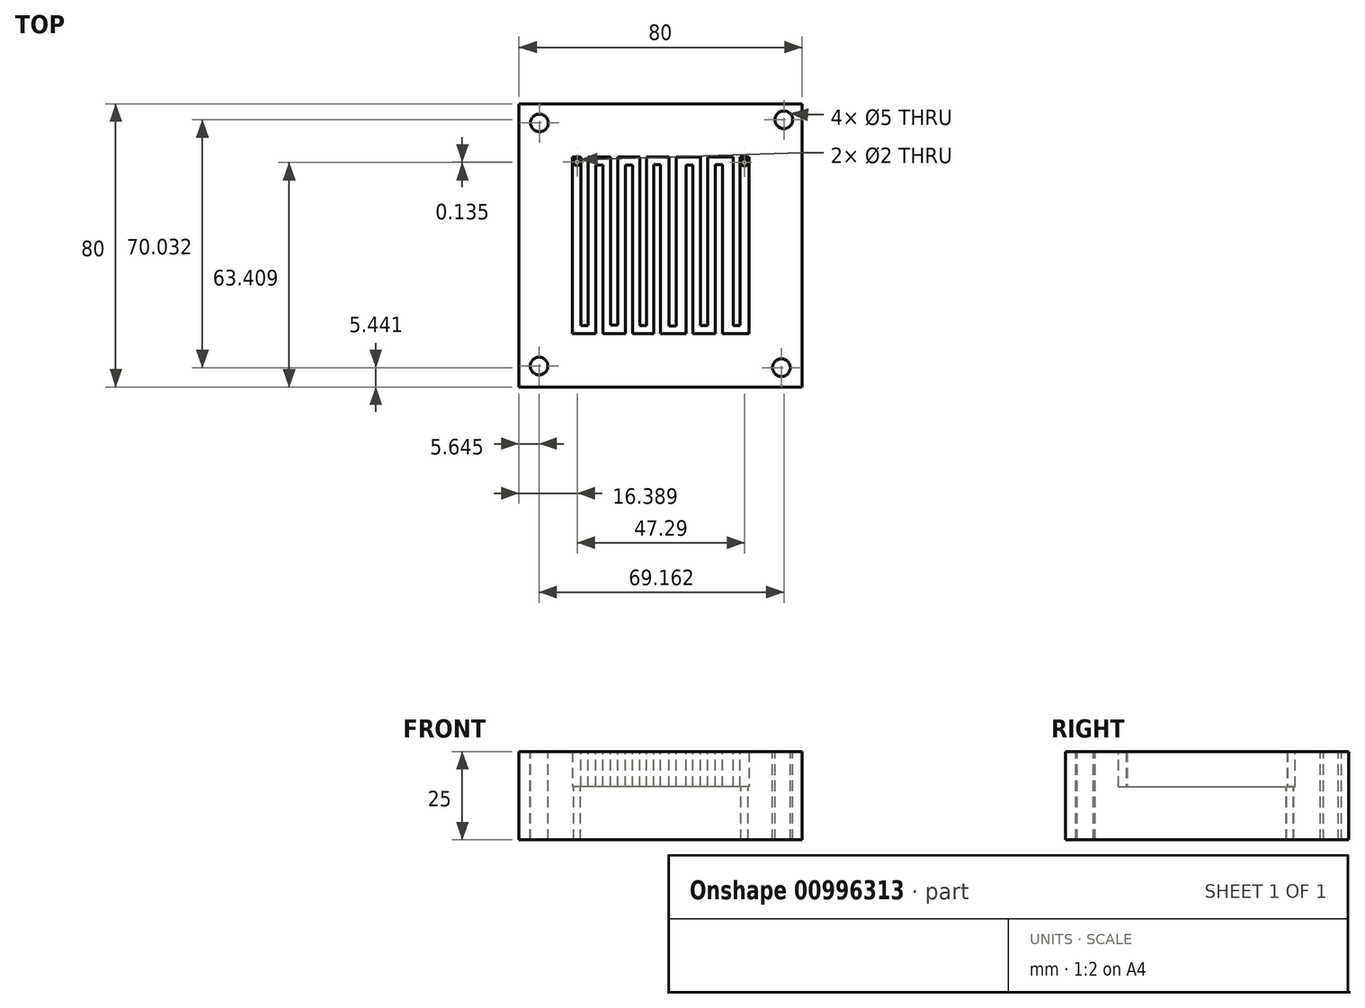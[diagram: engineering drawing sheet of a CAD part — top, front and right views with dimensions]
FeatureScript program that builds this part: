
annotation { "Feature Type Name" : "Feature", "Feature Type Description" : "" }
export const myFeature = defineFeature(function(context is Context, id is Id, definition is map)
    precondition{}
    {
        {
            var Q0;
            Q0=qCreatedBy(makeId("Top.planeOp"),FACE);
            var sketch = newSketch(context, id + "F0", { "sketchPlane" : qUnion([Q0])});
            skLineSegment(sketch, "E0.bottom", {"start": v(40, -40) * mm, "end": v(-40, -40) * mm});
            skLineSegment(sketch, "E0.top", {"start": v(40, 40) * mm, "end": v(-40, 40) * mm});
            skLineSegment(sketch, "E0.left", {"start": v(40, -40) * mm, "end": v(40, 40) * mm});
            skLineSegment(sketch, "E0.right", {"start": v(-40, -40) * mm, "end": v(-40, 40) * mm});
            skPoint(sketch, "E0.middle", {"position": v(0, 0) * mm});
            skSolve(sketch);
        }
        {
            var Q0;
            Q0=makeQuery(id+"F0.imprint","IMPRINT",FACE,{"disambiguationData":[TD([[makeQuery(id+"F0.imprint","IMPRINT",EDGE,{"derivedFrom":sQuery(id+"F0.wireOp",EDGE,"E0.bottom")}),-1.0]])]});
            var sketch = newSketch(context, id + "F1", { "sketchPlane" : qUnion([Q0])});
            skLineSegment(sketch, "E1.bottom", {"start": v(-22.53, 25.3) * mm, "end": v(-20.53, 25.3) * mm});
            skLineSegment(sketch, "E1.top", {"start": v(-22.53, -22.7) * mm, "end": v(-20.53, -22.7) * mm});
            skLineSegment(sketch, "E1.left", {"start": v(-22.53, 25.3) * mm, "end": v(-22.53, -22.7) * mm});
            skLineSegment(sketch, "E1.right", {"start": v(-20.53, 25.3) * mm, "end": v(-20.53, -22.7) * mm});
            skSolve(sketch);
        }
        {
            var Q0;
            Q0=makeQuery(id+"F0.imprint","IMPRINT",FACE,{"disambiguationData":[TD([[makeQuery(id+"F0.imprint","IMPRINT",EDGE,{"derivedFrom":sQuery(id+"F0.wireOp",EDGE,"E0.bottom")}),-1.0]])]});
            var sketch = newSketch(context, id + "F2", { "sketchPlane" : qUnion([Q0])});
            skLineSegment(sketch, "E2.bottom", {"start": v(-18.36, 22.64) * mm, "end": v(-16.36, 22.64) * mm});
            skLineSegment(sketch, "E2.top", {"start": v(-18.36, -25.36) * mm, "end": v(-16.36, -25.36) * mm});
            skLineSegment(sketch, "E2.left", {"start": v(-18.36, 22.64) * mm, "end": v(-18.36, -25.36) * mm});
            skLineSegment(sketch, "E2.right", {"start": v(-16.36, 22.64) * mm, "end": v(-16.36, -25.36) * mm});
            skLineSegment(sketch, "E3.bottom", {"start": v(-14.16, 25.43) * mm, "end": v(-12.16, 25.43) * mm});
            skLineSegment(sketch, "E3.top", {"start": v(-14.16, -22.57) * mm, "end": v(-12.16, -22.57) * mm});
            skLineSegment(sketch, "E3.left", {"start": v(-14.16, 25.43) * mm, "end": v(-14.16, -22.57) * mm});
            skLineSegment(sketch, "E3.right", {"start": v(-12.16, 25.43) * mm, "end": v(-12.16, -22.57) * mm});
            skLineSegment(sketch, "E4.bottom", {"start": v(-9.98, 22.64) * mm, "end": v(-7.98, 22.64) * mm});
            skLineSegment(sketch, "E4.top", {"start": v(-9.98, -25.36) * mm, "end": v(-7.98, -25.36) * mm});
            skLineSegment(sketch, "E4.left", {"start": v(-9.98, 22.64) * mm, "end": v(-9.98, -25.36) * mm});
            skLineSegment(sketch, "E4.right", {"start": v(-7.98, 22.64) * mm, "end": v(-7.98, -25.36) * mm});
            skLineSegment(sketch, "E5.bottom", {"start": v(-5.94, 25.3) * mm, "end": v(-3.94, 25.3) * mm});
            skLineSegment(sketch, "E5.top", {"start": v(-5.94, -22.7) * mm, "end": v(-3.94, -22.7) * mm});
            skLineSegment(sketch, "E5.left", {"start": v(-5.94, 25.3) * mm, "end": v(-5.94, -22.7) * mm});
            skLineSegment(sketch, "E5.right", {"start": v(-3.94, 25.3) * mm, "end": v(-3.94, -22.7) * mm});
            skLineSegment(sketch, "E6.bottom", {"start": v(-2, 22.77) * mm, "end": v(0, 22.77) * mm});
            skLineSegment(sketch, "E6.top", {"start": v(-2, -25.23) * mm, "end": v(0, -25.23) * mm});
            skLineSegment(sketch, "E6.left", {"start": v(-2, 22.77) * mm, "end": v(-2, -25.23) * mm});
            skLineSegment(sketch, "E6.right", {"start": v(0, 22.77) * mm, "end": v(0, -25.23) * mm});
            skLineSegment(sketch, "E7.bottom", {"start": v(2.41, 25.16) * mm, "end": v(4.41, 25.16) * mm});
            skLineSegment(sketch, "E7.top", {"start": v(2.41, -22.84) * mm, "end": v(4.41, -22.84) * mm});
            skLineSegment(sketch, "E7.left", {"start": v(2.41, 25.16) * mm, "end": v(2.41, -22.84) * mm});
            skLineSegment(sketch, "E7.right", {"start": v(4.41, 25.16) * mm, "end": v(4.41, -22.84) * mm});
            skLineSegment(sketch, "E8.bottom", {"start": v(7.13, 22.64) * mm, "end": v(9.13, 22.64) * mm});
            skLineSegment(sketch, "E8.top", {"start": v(7.13, -25.36) * mm, "end": v(9.13, -25.36) * mm});
            skLineSegment(sketch, "E8.left", {"start": v(7.13, 22.64) * mm, "end": v(7.13, -25.36) * mm});
            skLineSegment(sketch, "E8.right", {"start": v(9.13, 22.64) * mm, "end": v(9.13, -25.36) * mm});
            skLineSegment(sketch, "E9.bottom", {"start": v(11.3, 25.33) * mm, "end": v(13.3, 25.33) * mm});
            skLineSegment(sketch, "E9.top", {"start": v(11.3, -22.67) * mm, "end": v(13.3, -22.67) * mm});
            skLineSegment(sketch, "E9.left", {"start": v(11.3, 25.33) * mm, "end": v(11.3, -22.67) * mm});
            skLineSegment(sketch, "E9.right", {"start": v(13.3, 25.33) * mm, "end": v(13.3, -22.67) * mm});
            skLineSegment(sketch, "E10.bottom", {"start": v(15.48, 22.77) * mm, "end": v(17.48, 22.77) * mm});
            skLineSegment(sketch, "E10.top", {"start": v(15.48, -25.23) * mm, "end": v(17.48, -25.23) * mm});
            skLineSegment(sketch, "E10.left", {"start": v(15.48, 22.77) * mm, "end": v(15.48, -25.23) * mm});
            skLineSegment(sketch, "E10.right", {"start": v(17.48, 22.77) * mm, "end": v(17.48, -25.23) * mm});
            skLineSegment(sketch, "E11.bottom", {"start": v(20.47, 25.33) * mm, "end": v(22.47, 25.33) * mm});
            skLineSegment(sketch, "E11.top", {"start": v(20.47, -22.67) * mm, "end": v(22.47, -22.67) * mm});
            skLineSegment(sketch, "E11.left", {"start": v(20.47, 25.33) * mm, "end": v(20.47, -22.67) * mm});
            skLineSegment(sketch, "E11.right", {"start": v(22.47, 25.33) * mm, "end": v(22.47, -22.67) * mm});
            skSolve(sketch);
        }
        {
            var Q0;
            Q0 = qSketchRegion(id + "F0", true);
            extrude(context, id + "F3", {"entities" : qUnion([Q0]), "depth" : 25 * mm, "offsetDistance" : 25 * mm});
        }
        {
            var Q0;
            Q0=makeQuery(id+"F3.opExtrude","CAP_FACE",FACE,{"disambiguationData":[OSD([sQuery(id+"F0.wireOp",EDGE,"E0.bottom"),sQuery(id+"F0.wireOp",EDGE,"E0.top"),sQuery(id+"F0.wireOp",EDGE,"E0.left"),sQuery(id+"F0.wireOp",EDGE,"E0.right")])],"isStart":false});
            shell(context, id + "F4", {"entities" : qUnion([Q0]), "thickness" : 15 * mm});
        }
        {
            var Q0;
            Q0=makeQuery(id+"F4.opShell","OFFSET_FACE",FACE,{"disambiguationData":[OSD([sQuery(id+"F0.wireOp",EDGE,"E0.bottom"),sQuery(id+"F0.wireOp",EDGE,"E0.top"),sQuery(id+"F0.wireOp",EDGE,"E0.left"),sQuery(id+"F0.wireOp",EDGE,"E0.right")])]});
            var sketch = newSketch(context, id + "F5", { "sketchPlane" : qUnion([Q0])});
            skCircle(sketch, "E12", {"center": v(-23.61, 23.54) * mm, "radius": 0.81 * mm});
            skCircle(sketch, "E13", {"center": v(23.68, 23.4) * mm, "radius": 0.81 * mm});
            skSolve(sketch);
        }
        {
            var Q0;
            Q0 = qSketchRegion(id + "F1", true);
            var Q1;
            Q1 = qSketchRegion(id + "F2", true);
            extrude(context, id + "F6", {"entities" : qUnion([Q0, Q1]), "operationType" : NewBodyOperationType.ADD, "depth" : 25 * mm, "offsetDistance" : 25 * mm});
        }
        {
            var Q0;
            Q0=sQuery(id+"F5.wireOp",VERTEX,"E12.center");
            var Q1;
            Q1=sQuery(id+"F5.wireOp",VERTEX,"E13.center");
            var Q2;
            Q2=makeQuery(id+"F3.opExtrude","SWEPT_BODY",BODY,{"disambiguationData":[OSD([sQuery(id+"F0.wireOp",EDGE,"E0.bottom"),sQuery(id+"F0.wireOp",EDGE,"E0.top"),sQuery(id+"F0.wireOp",EDGE,"E0.left"),sQuery(id+"F0.wireOp",EDGE,"E0.right")])]});
            hole(context, id + "F7", {"style" : HoleStyle.SIMPLE, "endStyle" : HoleEndStyle.THROUGH, "holeDiameter" : 2 * mm, "majorDiameter" : 5 * mm, "isTappedThrough" : true, "tappedDepth" : 12 * mm, "tapClearance" : 3, "locations" : qUnion([Q0, Q1]), "scope" : qUnion([Q2])});
        }
        {
            var Q0;
            Q0=makeQuery(id+"F6.boolean.opBoolean","MERGE",FACE,{"derivedFrom":[makeQuery(id+"F3.opExtrude","CAP_FACE",FACE,{"disambiguationData":[OSD([sQuery(id+"F0.wireOp",EDGE,"E0.bottom"),sQuery(id+"F0.wireOp",EDGE,"E0.top"),sQuery(id+"F0.wireOp",EDGE,"E0.left"),sQuery(id+"F0.wireOp",EDGE,"E0.right")])],"isStart":false}),makeQuery(id+"F6.opExtrude","CAP_FACE",FACE,{"disambiguationData":[OSD([sQuery(id+"F1.wireOp",EDGE,"E1.bottom"),sQuery(id+"F1.wireOp",EDGE,"E1.top"),sQuery(id+"F1.wireOp",EDGE,"E1.left"),sQuery(id+"F1.wireOp",EDGE,"E1.right")])],"isStart":false}),makeQuery(id+"F6.opExtrude","CAP_FACE",FACE,{"disambiguationData":[OSD([sQuery(id+"F2.wireOp",EDGE,"E2.bottom"),sQuery(id+"F2.wireOp",EDGE,"E2.top"),sQuery(id+"F2.wireOp",EDGE,"E2.left"),sQuery(id+"F2.wireOp",EDGE,"E2.right")])],"isStart":false}),makeQuery(id+"F6.opExtrude","CAP_FACE",FACE,{"disambiguationData":[OSD([sQuery(id+"F2.wireOp",EDGE,"E3.bottom"),sQuery(id+"F2.wireOp",EDGE,"E3.top"),sQuery(id+"F2.wireOp",EDGE,"E3.left"),sQuery(id+"F2.wireOp",EDGE,"E3.right")])],"isStart":false}),makeQuery(id+"F6.opExtrude","CAP_FACE",FACE,{"disambiguationData":[OSD([sQuery(id+"F2.wireOp",EDGE,"E4.bottom"),sQuery(id+"F2.wireOp",EDGE,"E4.top"),sQuery(id+"F2.wireOp",EDGE,"E4.left"),sQuery(id+"F2.wireOp",EDGE,"E4.right")])],"isStart":false}),makeQuery(id+"F6.opExtrude","CAP_FACE",FACE,{"disambiguationData":[OSD([sQuery(id+"F2.wireOp",EDGE,"E5.bottom"),sQuery(id+"F2.wireOp",EDGE,"E5.top"),sQuery(id+"F2.wireOp",EDGE,"E5.left"),sQuery(id+"F2.wireOp",EDGE,"E5.right")])],"isStart":false}),makeQuery(id+"F6.opExtrude","CAP_FACE",FACE,{"disambiguationData":[OSD([sQuery(id+"F2.wireOp",EDGE,"E6.bottom"),sQuery(id+"F2.wireOp",EDGE,"E6.top"),sQuery(id+"F2.wireOp",EDGE,"E6.left"),sQuery(id+"F2.wireOp",EDGE,"E6.right")])],"isStart":false}),makeQuery(id+"F6.opExtrude","CAP_FACE",FACE,{"disambiguationData":[OSD([sQuery(id+"F2.wireOp",EDGE,"E7.bottom"),sQuery(id+"F2.wireOp",EDGE,"E7.top"),sQuery(id+"F2.wireOp",EDGE,"E7.left"),sQuery(id+"F2.wireOp",EDGE,"E7.right")])],"isStart":false}),makeQuery(id+"F6.opExtrude","CAP_FACE",FACE,{"disambiguationData":[OSD([sQuery(id+"F2.wireOp",EDGE,"E8.bottom"),sQuery(id+"F2.wireOp",EDGE,"E8.top"),sQuery(id+"F2.wireOp",EDGE,"E8.left"),sQuery(id+"F2.wireOp",EDGE,"E8.right")])],"isStart":false}),makeQuery(id+"F6.opExtrude","CAP_FACE",FACE,{"disambiguationData":[OSD([sQuery(id+"F2.wireOp",EDGE,"E9.bottom"),sQuery(id+"F2.wireOp",EDGE,"E9.top"),sQuery(id+"F2.wireOp",EDGE,"E9.left"),sQuery(id+"F2.wireOp",EDGE,"E9.right")])],"isStart":false}),makeQuery(id+"F6.opExtrude","CAP_FACE",FACE,{"disambiguationData":[OSD([sQuery(id+"F2.wireOp",EDGE,"E10.bottom"),sQuery(id+"F2.wireOp",EDGE,"E10.top"),sQuery(id+"F2.wireOp",EDGE,"E10.left"),sQuery(id+"F2.wireOp",EDGE,"E10.right")])],"isStart":false}),makeQuery(id+"F6.opExtrude","CAP_FACE",FACE,{"disambiguationData":[OSD([sQuery(id+"F2.wireOp",EDGE,"E11.bottom"),sQuery(id+"F2.wireOp",EDGE,"E11.top"),sQuery(id+"F2.wireOp",EDGE,"E11.left"),sQuery(id+"F2.wireOp",EDGE,"E11.right")])],"isStart":false})]});
            var sketch = newSketch(context, id + "F8", { "sketchPlane" : qUnion([Q0])});
            skCircle(sketch, "E14", {"center": v(-34.26, 34.6) * mm, "radius": 2.97 * mm});
            skCircle(sketch, "E15", {"center": v(-34.36, -34.1) * mm, "radius": 2.97 * mm});
            skCircle(sketch, "E16", {"center": v(34.11, -34.56) * mm, "radius": 2.97 * mm});
            skCircle(sketch, "E17", {"center": v(34.8, 35.47) * mm, "radius": 2.97 * mm});
            skSolve(sketch);
        }
        {
            var Q0;
            Q0=sQuery(id+"F8.wireOp",VERTEX,"E14.center");
            var Q1;
            Q1=sQuery(id+"F8.wireOp",VERTEX,"E17.center");
            var Q2;
            Q2=sQuery(id+"F8.wireOp",VERTEX,"E16.center");
            var Q3;
            Q3=sQuery(id+"F8.wireOp",VERTEX,"E15.center");
            var Q4;
            Q4=makeQuery(id+"F3.opExtrude","SWEPT_BODY",BODY,{"disambiguationData":[OSD([sQuery(id+"F0.wireOp",EDGE,"E0.bottom"),sQuery(id+"F0.wireOp",EDGE,"E0.top"),sQuery(id+"F0.wireOp",EDGE,"E0.left"),sQuery(id+"F0.wireOp",EDGE,"E0.right")])]});
            hole(context, id + "F9", {"style" : HoleStyle.SIMPLE, "endStyle" : HoleEndStyle.THROUGH, "holeDiameter" : 5 * mm, "majorDiameter" : 5 * mm, "isTappedThrough" : true, "tappedDepth" : 12 * mm, "tapClearance" : 3, "locations" : qUnion([Q0, Q1, Q2, Q3]), "scope" : qUnion([Q4])});
        }
    });
